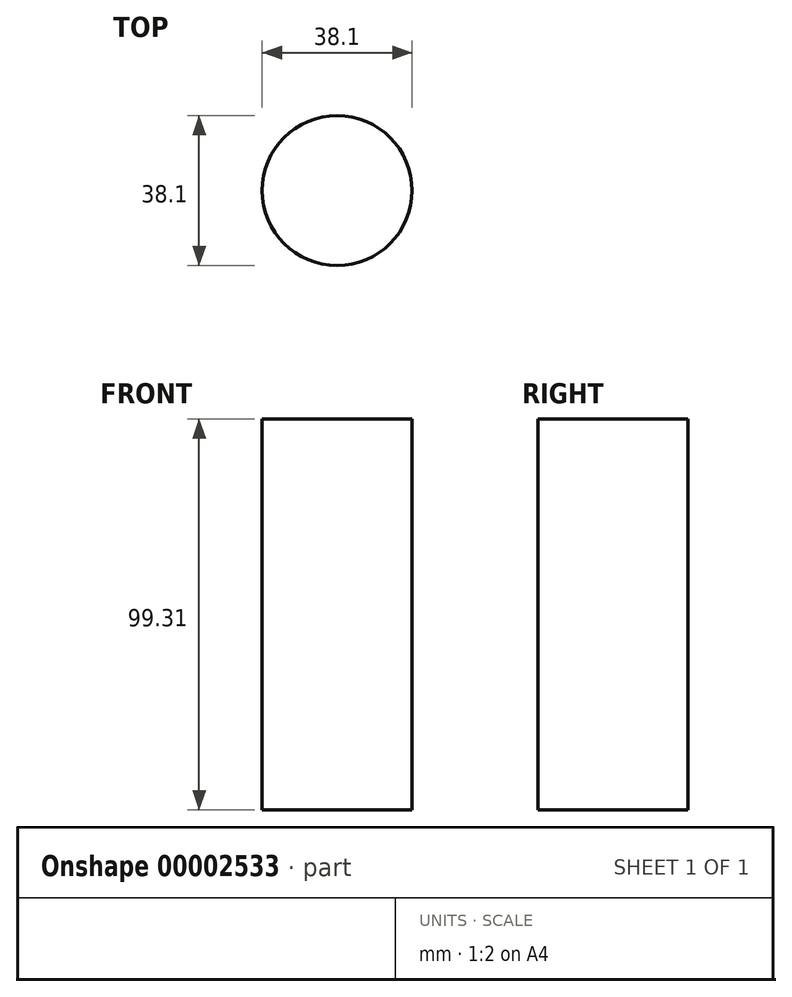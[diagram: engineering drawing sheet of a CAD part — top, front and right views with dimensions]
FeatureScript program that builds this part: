
annotation { "Feature Type Name" : "Feature", "Feature Type Description" : "" }
export const myFeature = defineFeature(function(context is Context, id is Id, definition is map)
    precondition{}
    {
        {
            var Q0;
            Q0=qCreatedBy(makeId("Top.planeOp"),FACE);
            var sketch = newSketch(context, id + "F0", { "sketchPlane" : qUnion([Q0])});
            skCircle(sketch, "E0", {"center": v(0, 0) * mm, "radius": 19.05 * mm});
            skSolve(sketch);
        }
        {
            var Q0;
            Q0=makeQuery(id+"F0.imprint","IMPRINT",FACE,{"disambiguationData":[TD([[makeQuery(id+"F0.imprint","IMPRINT",EDGE,{"derivedFrom":sQuery(id+"F0.wireOp",EDGE,"E0")}),1.0]])]});
            extrude(context, id + "F1", {"entities" : qUnion([Q0]), "depth" : 99.31 * mm, "offsetDistance" : 25.4 * mm});
        }
    });
